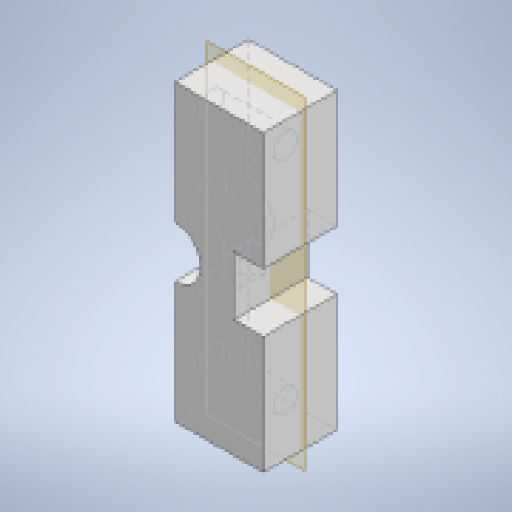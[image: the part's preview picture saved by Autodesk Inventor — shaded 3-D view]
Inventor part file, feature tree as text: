
AUTODESK INVENTOR PART (.ipt)
format: ipt  version: 2023 (Build 270158000, 158)  size: 184,320 bytes
history: native  units: mm
features: extrude x4, sketch x4, thread x2, plane x1
ambient origin geometry x8: Origin, YZ Plane, XZ Plane, XY Plane, X Axis, Y Axis, Z Axis, Center Point
bodies: Solid1 (feature_tree)
feature tree (11):
  extrude  "Extrusion1"  Depth=20.0mm
  plane  "Work Plane1"
  extrude  "Extrusion2"  Depth=2.0mm
  extrude  "Extrusion3"  Depth=4.0mm
  extrude  "Extrusion4"  Depth=5.0mm TaperAngle=0.0deg
  thread  "Thread1"  [1 undecoded]
  thread  "Thread2"  [1 undecoded]
  sketch  "Sketch1"  dims[d0=20.0mm d1=20.0mm]
  sketch  "Sketch2"  dims[d2=4.0mm d6=2.0mm]
  sketch  "Sketch3"  dims[d7=2.0mm d8=4.0mm]
  sketch  "Sketch4"  dims[d9=2.0mm d10=5.0mm d11=0.0mm d12=5.5mm d13=1.8mm d14=0.0mm d15=3.5mm d16=8.0mm d17=0.0mm d18=1.6mm d19=1.6mm d20=2.5mm d21=2.5mm d22=2.5mm d23=2.5mm d24=5.0mm d25=0.0mm d26=5.0mm d27=0.0mm d28=5.0mm d29=0.0mm]
note: 2 required parameter values undecoded (feature->parameter linkage not recoverable at this tier; creation-order binding heuristic only, values carry confidence <= 0.55)
